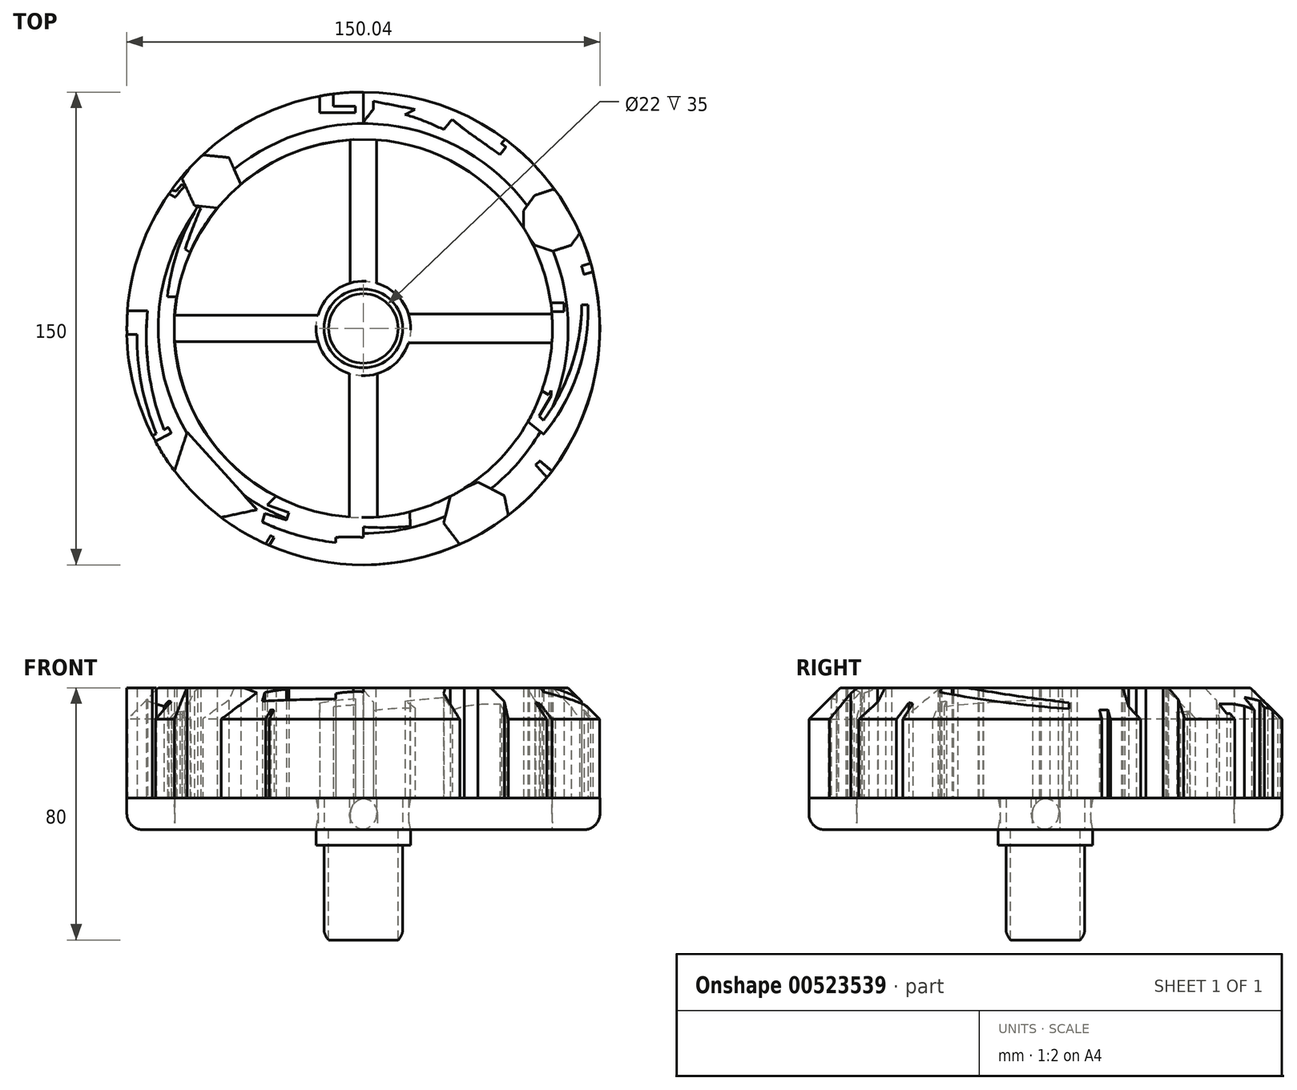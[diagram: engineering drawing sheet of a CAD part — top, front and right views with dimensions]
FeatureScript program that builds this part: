
annotation { "Feature Type Name" : "Feature", "Feature Type Description" : "" }
export const myFeature = defineFeature(function(context is Context, id is Id, definition is map)
    precondition{}
    {
        {
            var Q0;
            Q0=qCreatedBy(makeId("Top.planeOp"),FACE);
            var sketch = newSketch(context, id + "F0", { "sketchPlane" : qUnion([Q0])});
            skCircle(sketch, "E0", {"center": v(-0.06, 0) * mm, "radius": 75 * mm});
            skArc(sketch, "E1", {"start": v(-3.12, 59.92) * mm, "mid": v(-42.12, 42.8) * mm, "end": v(-59.92, 4.1) * mm});
            skArc(sketch, "E2.trimOffspring", {"start": v(59.92, 1.45) * mm, "mid": v(43.26, 41.51) * mm, "end": v(3.94, 59.87) * mm});
            skArc(sketch, "E3.trimOffspring", {"start": v(3.47, -59.9) * mm, "mid": v(43.1, -41.68) * mm, "end": v(59.92, -1.45) * mm});
            skArc(sketch, "E4.trimOffspring", {"start": v(-59.92, -4.1) * mm, "mid": v(-42.29, -42.63) * mm, "end": v(-3.6, -59.9) * mm});
            skLineSegment(sketch, "E5", {"start": v(-3.6, -59.9) * mm, "end": v(3.47, -59.9) * mm});
            skLineSegment(sketch, "E6", {"start": v(-59.92, 4.1) * mm, "end": v(-59.92, -4.1) * mm});
            skLineSegment(sketch, "E7", {"start": v(-3.12, 59.92) * mm, "end": v(3.94, 59.87) * mm});
            skLineSegment(sketch, "E8", {"start": v(59.92, 1.45) * mm, "end": v(59.92, -1.45) * mm});
            skLineSegment(sketch, "E9", {"start": v(-75.04, -1.85) * mm, "end": v(-71.81, -1.85) * mm});
            skArc(sketch, "E10", {"start": v(-71.81, -1.85) * mm, "mid": v(-70.32, -18.07) * mm, "end": v(-65.5, -33.64) * mm});
            skLineSegment(sketch, "E11", {"start": v(-65.5, -33.64) * mm, "end": v(-62.98, -32.75) * mm});
            skArc(sketch, "E12", {"start": v(-68.45, 5.56) * mm, "mid": v(-68, -13.92) * mm, "end": v(-62.98, -32.75) * mm});
            skLineSegment(sketch, "E13", {"start": v(-68.45, 5.56) * mm, "end": v(-74.86, 5.56) * mm});
            skLineSegment(sketch, "E14", {"start": v(-59.2, 10.09) * mm, "end": v(-62.16, 10.09) * mm});
            skArc(sketch, "E15", {"start": v(-52.57, 38.7) * mm, "mid": v(-58.84, 24.89) * mm, "end": v(-62.16, 10.09) * mm});
            skLineSegment(sketch, "E16", {"start": v(-52.57, 38.7) * mm, "end": v(-51.6, 38.07) * mm});
            skArc(sketch, "E17", {"start": v(-51.6, 38.07) * mm, "mid": v(-54.22, 31.64) * mm, "end": v(-56.54, 25.1) * mm});
            skCircle(sketch, "E18.cCircle", {"center": v(-51.93, -51.6) * mm, "radius": 9.56 * mm, "construction": true});
            skLineSegment(sketch, "E18.0", {"start": v(-55.9, -32.91) * mm, "end": v(-33.75, -57.52) * mm});
            skLineSegment(sketch, "E18.1", {"start": v(-33.75, -57.52) * mm, "end": v(-66.13, -64.4) * mm});
            skLineSegment(sketch, "E18.2", {"start": v(-66.13, -64.4) * mm, "end": v(-55.9, -32.91) * mm});
            skPoint(sketch, "E18.0.midPoint", {"position": v(-44.82, -45.21) * mm});
            skLineSegment(sketch, "E19", {"start": v(-27.68, -53.26) * mm, "end": v(-30.43, -56) * mm});
            skLineSegment(sketch, "E20", {"start": v(-23.66, -58.36) * mm, "end": v(-24.37, -60.74) * mm});
            skLineSegment(sketch, "E21", {"start": v(-24.37, -60.74) * mm, "end": v(-31.28, -58.71) * mm});
            skLineSegment(sketch, "E22", {"start": v(-31.28, -58.71) * mm, "end": v(-32.06, -61.39) * mm});
            skArc(sketch, "E23", {"start": v(-32.06, -61.39) * mm, "mid": v(-20.7, -65.62) * mm, "end": v(-8.8, -67.96) * mm});
            skLineSegment(sketch, "E24", {"start": v(-8.8, -67.96) * mm, "end": v(-8.8, -66.27) * mm});
            skArc(sketch, "E25", {"start": v(0, -66.27) * mm, "mid": v(-4.4, -66.16) * mm, "end": v(-8.8, -66.27) * mm});
            skLineSegment(sketch, "E26", {"start": v(0, -66.27) * mm, "end": v(0, -62.95) * mm});
            skArc(sketch, "E27", {"start": v(0, -62.95) * mm, "mid": v(5.89, -63.2) * mm, "end": v(11.77, -62.95) * mm});
            skLineSegment(sketch, "E28", {"start": v(11.77, -62.95) * mm, "end": v(14.82, -62.7) * mm});
            skLineSegment(sketch, "E29", {"start": v(14.82, -62.7) * mm, "end": v(14.7, -58.15) * mm});
            skCircle(sketch, "E30.cCircle", {"center": v(36.07, -59.58) * mm, "radius": 9.76 * mm, "construction": true});
            skLineSegment(sketch, "E30.0", {"start": v(27.76, -52.62) * mm, "end": v(36.33, -48.75) * mm});
            skLineSegment(sketch, "E30.1", {"start": v(36.33, -48.75) * mm, "end": v(44.7, -53.03) * mm});
            skLineSegment(sketch, "E30.2", {"start": v(44.7, -53.03) * mm, "end": v(46.57, -62.25) * mm});
            skLineSegment(sketch, "E30.3", {"start": v(46.57, -62.25) * mm, "end": v(40.53, -69.45) * mm});
            skLineSegment(sketch, "E30.4", {"start": v(40.53, -69.45) * mm, "end": v(31.13, -69.23) * mm});
            skLineSegment(sketch, "E30.5", {"start": v(31.13, -69.23) * mm, "end": v(25.45, -61.74) * mm});
            skLineSegment(sketch, "E30.6", {"start": v(25.45, -61.74) * mm, "end": v(27.76, -52.62) * mm});
            skPoint(sketch, "E30.0.midPoint", {"position": v(32.05, -50.69) * mm});
            skLineSegment(sketch, "E31", {"start": v(58.18, -47.25) * mm, "end": v(54.6, -43.25) * mm});
            skLineSegment(sketch, "E32", {"start": v(54.6, -43.25) * mm, "end": v(55.97, -42.03) * mm});
            skLineSegment(sketch, "E33", {"start": v(55.97, -42.03) * mm, "end": v(59.75, -45.25) * mm});
            skLineSegment(sketch, "E34", {"start": v(52.16, -29.54) * mm, "end": v(57.17, -33.54) * mm});
            skArc(sketch, "E35", {"start": v(57.17, -33.54) * mm, "mid": v(67.92, -14.28) * mm, "end": v(71.22, 7.53) * mm});
            skLineSegment(sketch, "E36", {"start": v(71.22, 7.53) * mm, "end": v(69.25, 7.53) * mm});
            skArc(sketch, "E37", {"start": v(57.08, -29.17) * mm, "mid": v(66.08, -11.78) * mm, "end": v(69.25, 7.53) * mm});
            skLineSegment(sketch, "E38", {"start": v(57.08, -29.17) * mm, "end": v(55.76, -27.85) * mm});
            skLineSegment(sketch, "E39", {"start": v(55.76, -27.85) * mm, "end": v(59.54, -21.34) * mm});
            skLineSegment(sketch, "E40", {"start": v(59.54, -21.34) * mm, "end": v(59.54, -19.73) * mm});
            skLineSegment(sketch, "E41", {"start": v(58.8, -21.06) * mm, "end": v(59.54, -19.73) * mm});
            skLineSegment(sketch, "E42", {"start": v(58.8, -21.06) * mm, "end": v(56.57, -19.82) * mm});
            skLineSegment(sketch, "E43", {"start": v(59.7, 5.3) * mm, "end": v(63.56, 5.3) * mm});
            skLineSegment(sketch, "E44", {"start": v(63.56, 5.3) * mm, "end": v(63.56, 8.1) * mm});
            skLineSegment(sketch, "E45", {"start": v(63.56, 8.1) * mm, "end": v(59.4, 8.1) * mm});
            skCircle(sketch, "E46.cCircle", {"center": v(60.08, 34.31) * mm, "radius": 9.31 * mm, "construction": true});
            skLineSegment(sketch, "E46.0", {"start": v(54.36, 26.37) * mm, "end": v(50.78, 31.25) * mm});
            skLineSegment(sketch, "E46.1", {"start": v(50.78, 31.25) * mm, "end": v(50.76, 37.3) * mm});
            skLineSegment(sketch, "E46.2", {"start": v(50.76, 37.3) * mm, "end": v(54.3, 42.21) * mm});
            skLineSegment(sketch, "E46.3", {"start": v(54.3, 42.21) * mm, "end": v(60.05, 44.1) * mm});
            skLineSegment(sketch, "E46.4", {"start": v(60.05, 44.1) * mm, "end": v(65.8, 42.25) * mm});
            skLineSegment(sketch, "E46.5", {"start": v(65.8, 42.25) * mm, "end": v(69.38, 37.37) * mm});
            skLineSegment(sketch, "E46.6", {"start": v(69.38, 37.37) * mm, "end": v(69.4, 31.32) * mm});
            skLineSegment(sketch, "E46.7", {"start": v(69.4, 31.32) * mm, "end": v(65.87, 26.41) * mm});
            skLineSegment(sketch, "E46.8", {"start": v(65.87, 26.41) * mm, "end": v(60.12, 24.52) * mm});
            skLineSegment(sketch, "E46.9", {"start": v(60.12, 24.52) * mm, "end": v(54.36, 26.37) * mm});
            skPoint(sketch, "E46.0.midPoint", {"position": v(52.57, 28.81) * mm});
            skLineSegment(sketch, "E47", {"start": v(72.04, 20.65) * mm, "end": v(69.17, 19.85) * mm});
            skLineSegment(sketch, "E48", {"start": v(69.17, 19.85) * mm, "end": v(69.92, 17.15) * mm});
            skLineSegment(sketch, "E49", {"start": v(69.92, 17.15) * mm, "end": v(72.76, 17.95) * mm});
            skLineSegment(sketch, "E50", {"start": v(-29.91, -68.8) * mm, "end": v(-28.39, -66.32) * mm});
            skLineSegment(sketch, "E51", {"start": v(-28.39, -66.32) * mm, "end": v(-29.4, -65.7) * mm});
            skLineSegment(sketch, "E52", {"start": v(-29.4, -65.7) * mm, "end": v(-31, -68.32) * mm});
            skLineSegment(sketch, "E53", {"start": v(-66.9, -34) * mm, "end": v(-61.84, -31.39) * mm});
            skLineSegment(sketch, "E54", {"start": v(-61.84, -31.39) * mm, "end": v(-60.9, -33.2) * mm});
            skLineSegment(sketch, "E55", {"start": v(-60.9, -33.2) * mm, "end": v(-65.96, -35.8) * mm});
            skCircle(sketch, "E56.cCircle", {"center": v(-48.13, 46.59) * mm, "radius": 8.14 * mm, "construction": true});
            skLineSegment(sketch, "E56.0", {"start": v(-57.48, 47.52) * mm, "end": v(-52, 55.15) * mm});
            skLineSegment(sketch, "E56.1", {"start": v(-52, 55.15) * mm, "end": v(-42.65, 54.21) * mm});
            skLineSegment(sketch, "E56.2", {"start": v(-42.65, 54.21) * mm, "end": v(-38.79, 45.65) * mm});
            skLineSegment(sketch, "E56.3", {"start": v(-38.79, 45.65) * mm, "end": v(-44.27, 38.02) * mm});
            skLineSegment(sketch, "E56.4", {"start": v(-44.27, 38.02) * mm, "end": v(-53.62, 38.96) * mm});
            skLineSegment(sketch, "E56.5", {"start": v(-53.62, 38.96) * mm, "end": v(-57.48, 47.52) * mm});
            skPoint(sketch, "E56.0.midPoint", {"position": v(-54.74, 51.34) * mm});
            skLineSegment(sketch, "E57", {"start": v(-56.54, 25.1) * mm, "end": v(-55, 24.11) * mm});
            skLineSegment(sketch, "E58", {"start": v(-61.7, 42.74) * mm, "end": v(-59.66, 41.61) * mm});
            skLineSegment(sketch, "E59", {"start": v(-59.66, 41.61) * mm, "end": v(-58.14, 43.52) * mm});
            skLineSegment(sketch, "E60", {"start": v(-58.14, 43.52) * mm, "end": v(-56.83, 45) * mm});
            skLineSegment(sketch, "E61", {"start": v(-56.83, 45) * mm, "end": v(-57.59, 45.67) * mm});
            skLineSegment(sketch, "E62", {"start": v(-57.59, 45.67) * mm, "end": v(-59.43, 43.57) * mm});
            skLineSegment(sketch, "E63", {"start": v(-59.43, 43.57) * mm, "end": v(-60.85, 43.92) * mm});
            skLineSegment(sketch, "E64", {"start": v(45.17, 57.51) * mm, "end": v(43.33, 55.14) * mm});
            skLineSegment(sketch, "E65", {"start": v(43.33, 55.14) * mm, "end": v(32.11, 63.08) * mm});
            skLineSegment(sketch, "E66", {"start": v(0, 65.39) * mm, "end": v(0, 75) * mm});
            skArc(sketch, "E67", {"start": v(3.13, 69.5) * mm, "mid": v(1.52, 67.47) * mm, "end": v(0, 65.39) * mm});
            skLineSegment(sketch, "E68", {"start": v(3.13, 69.5) * mm, "end": v(3.13, 72.11) * mm});
            skLineSegment(sketch, "E69", {"start": v(3.13, 72.11) * mm, "end": v(16.41, 69.5) * mm});
            skLineSegment(sketch, "E70", {"start": v(16.41, 69.5) * mm, "end": v(13.26, 67.89) * mm});
            skArc(sketch, "E71", {"start": v(25.48, 63.08) * mm, "mid": v(19.47, 65.74) * mm, "end": v(13.26, 67.89) * mm});
            skLineSegment(sketch, "E72", {"start": v(25.48, 63.08) * mm, "end": v(28.14, 66.33) * mm});
            skLineSegment(sketch, "E73", {"start": v(28.14, 66.33) * mm, "end": v(32.11, 63.08) * mm});
            skLineSegment(sketch, "E74", {"start": v(65.58, 40.81) * mm, "end": v(66.25, 41.64) * mm});
            skLineSegment(sketch, "E75", {"start": v(62.54, 43.3) * mm, "end": v(65.58, 40.81) * mm});
            skLineSegment(sketch, "E76", {"start": v(43.79, 58.64) * mm, "end": v(44.91, 60.02) * mm});
            skLineSegment(sketch, "E77", {"start": v(-9.57, 74.4) * mm, "end": v(-9.57, 70.46) * mm});
            skLineSegment(sketch, "E78", {"start": v(-9.57, 70.46) * mm, "end": v(-2.58, 70.46) * mm});
            skLineSegment(sketch, "E79", {"start": v(-2.58, 70.46) * mm, "end": v(-2.58, 68.43) * mm});
            skLineSegment(sketch, "E80", {"start": v(-2.58, 68.43) * mm, "end": v(-9.37, 68.43) * mm});
            skLineSegment(sketch, "E81", {"start": v(-9.37, 68.43) * mm, "end": v(-13.9, 68.43) * mm});
            skLineSegment(sketch, "E82", {"start": v(-13.9, 68.43) * mm, "end": v(-13.9, 73.71) * mm});
            skArc(sketch, "E83", {"start": v(-27.44, 58.39) * mm, "mid": v(-46.31, 48.67) * mm, "end": v(-54.8, 29.21) * mm});
            skLineSegment(sketch, "E84", {"start": v(-27.44, 58.39) * mm, "end": v(-27.44, 62.14) * mm});
            skArc(sketch, "E85", {"start": v(-27.44, 62.14) * mm, "mid": v(-37.43, 59.53) * mm, "end": v(-46.73, 55.07) * mm});
            skLineSegment(sketch, "E86.trimOffspring", {"start": v(43.79, 58.64) * mm, "end": v(45.17, 57.51) * mm});
            skLineSegment(sketch, "E87", {"start": v(-30.43, -56) * mm, "end": v(-23.66, -58.36) * mm});
            skSolve(sketch);
        }
        {
            var Q0;
            Q0=qCreatedBy(makeId("Top.planeOp"),FACE);
            var sketch = newSketch(context, id + "F1", { "sketchPlane" : qUnion([Q0])});
            skCircle(sketch, "E88", {"center": v(0, 0) * mm, "radius": 11 * mm});
            skCircle(sketch, "E89", {"center": v(0, 0) * mm, "radius": 12.5 * mm});
            skCircle(sketch, "E90", {"center": v(0, 0) * mm, "radius": 75 * mm});
            skCircle(sketch, "E91", {"center": v(0, 0) * mm, "radius": 60 * mm});
            skLineSegment(sketch, "E92", {"start": v(-11.79, 4.17) * mm, "end": v(-59.86, 4.17) * mm});
            skLineSegment(sketch, "E93", {"start": v(-11.79, -4.17) * mm, "end": v(-59.86, -4.17) * mm});
            skLineSegment(sketch, "E94", {"start": v(-4.17, 59.86) * mm, "end": v(-4.17, 11.79) * mm});
            skLineSegment(sketch, "E95", {"start": v(4.17, 11.79) * mm, "end": v(4.17, 59.86) * mm});
            skLineSegment(sketch, "E96.MirrorCS", {"start": v(11.58, 4.52) * mm, "end": v(59.83, 4.52) * mm});
            skLineSegment(sketch, "E97.MirrorCS", {"start": v(11.58, -4.52) * mm, "end": v(59.83, -4.52) * mm});
            skLineSegment(sketch, "E98.MirrorCS", {"start": v(-4.47, -59.83) * mm, "end": v(-4.41, -11.7) * mm});
            skLineSegment(sketch, "E99.MirrorCS", {"start": v(4.41, -11.7) * mm, "end": v(4.47, -59.83) * mm});
            skSolve(sketch);
        }
        {
            var Q0;
            Q0=qCreatedBy(makeId("Top.planeOp"),FACE);
            var sketch = newSketch(context, id + "F2", { "sketchPlane" : qUnion([Q0])});
            skCircle(sketch, "E100", {"center": v(0, 0) * mm, "radius": 12.5 * mm});
            skCircle(sketch, "E101", {"center": v(0, 0) * mm, "radius": 15 * mm});
            skSolve(sketch);
        }
        {
            var Q0;
            Q0=qCreatedBy(makeId("Top.planeOp"),FACE);
            var sketch = newSketch(context, id + "F3", { "sketchPlane" : qUnion([Q0])});
            skCircle(sketch, "E102", {"center": v(0, 0) * mm, "radius": 11 * mm});
            skCircle(sketch, "E103", {"center": v(0, 0) * mm, "radius": 12.5 * mm});
            skSolve(sketch);
        }
        {
            var Q0;
            {var subQ9=sQuery(id+"F0.wireOp",EDGE,"E6");Q0=makeQuery(id+"F0.imprint","IMPRINT",FACE,{"disambiguationData":[TD([[makeQuery(id+"F0.imprint","IMPRINT",EDGE,{"derivedFrom":subQ9}),-1.0]])]});}
            var Q1;
            {var subQ12=sQuery(id+"F0.wireOp",EDGE,"E7");Q1=makeQuery(id+"F0.imprint","IMPRINT",FACE,{"disambiguationData":[TD([[makeQuery(id+"F0.imprint","IMPRINT",EDGE,{"derivedFrom":subQ12}),1.0]])]});}
            var Q2;
            {var subQ7=sQuery(id+"F0.wireOp",EDGE,"E8");Q2=makeQuery(id+"F0.imprint","IMPRINT",FACE,{"disambiguationData":[TD([[makeQuery(id+"F0.imprint","IMPRINT",EDGE,{"derivedFrom":subQ7}),1.0]])]});}
            var Q3;
            {var subQ0=sQuery(id+"F0.wireOp",EDGE,"E9");Q3=makeQuery(id+"F0.imprint","IMPRINT",FACE,{"disambiguationData":[TD([[makeQuery(id+"F0.imprint","IMPRINT",EDGE,{"derivedFrom":subQ0}),-1.0]])]});}
            var Q4;
            {var subQ1=sQuery(id+"F0.wireOp",EDGE,"E16");Q4=makeQuery(id+"F0.imprint","IMPRINT",FACE,{"disambiguationData":[TD([[makeQuery(id+"F0.imprint","IMPRINT",EDGE,{"derivedFrom":subQ1}),1.0]])]});}
            extrude(context, id + "F4", {"entities" : qUnion([Q0, Q1, Q2, Q3, Q4]), "depth" : 45 * mm, "offsetDistance" : 25 * mm, "hasSecondDirection" : true, "secondDirectionOppositeDirection" : false, "secondDirectionDepth" : 10 * mm});
        }
        {
            var Q0;
            Q0=makeQuery(id+"F2.imprint","IMPRINT",FACE,{"disambiguationData":[TD([[makeQuery(id+"F2.imprint","IMPRINT",EDGE,{"derivedFrom":sQuery(id+"F2.wireOp",EDGE,"E100")}),-1.0]])]});
            var Q1;
            {var subQ0=sQuery(id+"F1.wireOp",EDGE,"E94");Q1=makeQuery(id+"F1.imprint","IMPRINT",FACE,{"disambiguationData":[TD([[makeQuery(id+"F1.imprint","IMPRINT",EDGE,{"derivedFrom":subQ0}),1.0]])]});}
            var Q2;
            {var subQ0=sQuery(id+"F1.wireOp",EDGE,"E92");Q2=makeQuery(id+"F1.imprint","IMPRINT",FACE,{"disambiguationData":[TD([[makeQuery(id+"F1.imprint","IMPRINT",EDGE,{"derivedFrom":subQ0}),1.0]])]});}
            var Q3;
            Q3=makeQuery(id+"F1.imprint","IMPRINT",FACE,{"disambiguationData":[TD([[makeQuery(id+"F1.imprint","IMPRINT",EDGE,{"derivedFrom":sQuery(id+"F1.wireOp",EDGE,"E90")}),1.0]])]});
            var Q4;
            {var subQ0=sQuery(id+"F1.wireOp",EDGE,"E96.MirrorCS");var subQ1=sQuery(id+"F1.wireOp",EDGE,"E89");var subQ2=makeQuery(id+"F1.imprint","INTERSECT",VERTEX,{"derivedFrom":[subQ1,subQ0]});Q4=makeQuery(id+"F1.imprint","IMPRINT",FACE,{"disambiguationData":[TD([[makeQuery(id+"F1.imprint","IMPRINT",EDGE,{"disambiguationData":[TD([[subQ2,1.0]])],"derivedFrom":subQ1}),-1.0]])]});}
            var Q5;
            {var subQ0=sQuery(id+"F1.wireOp",EDGE,"E98.MirrorCS");Q5=makeQuery(id+"F1.imprint","IMPRINT",FACE,{"disambiguationData":[TD([[makeQuery(id+"F1.imprint","IMPRINT",EDGE,{"derivedFrom":subQ0}),-1.0]])]});}
            extrude(context, id + "F5", {"entities" : qUnion([Q0, Q1, Q2, Q3, Q4, Q5]), "operationType" : NewBodyOperationType.ADD, "depth" : 10 * mm, "offsetDistance" : 25 * mm});
        }
        {
            var Q0;
            Q0 = qSketchRegion(id + "F2", true);
            extrude(context, id + "F6", {"entities" : qUnion([Q0]), "operationType" : NewBodyOperationType.ADD, "oppositeDirection" : true, "depth" : 5 * mm, "offsetDistance" : 25 * mm});
        }
        {
            var Q0;
            Q0 = qSketchRegion(id + "F3", true);
            extrude(context, id + "F7", {"entities" : qUnion([Q0]), "operationType" : NewBodyOperationType.ADD, "oppositeDirection" : true, "depth" : 35 * mm, "offsetDistance" : 25 * mm});
        }
        {
            var Q0;
            Q0=makeQuery(id+"F5.opExtrude","CAP_EDGE",EDGE,{"disambiguationData":[OSD([sQuery(id+"F1.wireOp",EDGE,"E93")])],"isStart":false});
            var Q1;
            {var subQ0=sQuery(id+"F2.wireOp",EDGE,"E101");var subQ1=sQuery(id+"F1.wireOp",EDGE,"E92");var subQ2=sQuery(id+"F1.wireOp",EDGE,"E91");var subQ3=sQuery(id+"F1.wireOp",EDGE,"E94");var subQ4=makeQuery(id+"F5.opExtrude","SWEPT_FACE",FACE,{"disambiguationData":[OSD([subQ1])]});var subQ5=makeQuery(id+"F5.opExtrude","CAP_FACE",FACE,{"disambiguationData":[OSD([sQuery(id+"F1.wireOp",EDGE,"E88"),sQuery(id+"F1.wireOp",EDGE,"E89"),sQuery(id+"F1.wireOp",EDGE,"E90"),subQ2,subQ1,sQuery(id+"F1.wireOp",EDGE,"E93"),subQ3,sQuery(id+"F1.wireOp",EDGE,"E95"),sQuery(id+"F1.wireOp",EDGE,"E96.MirrorCS"),sQuery(id+"F1.wireOp",EDGE,"E97.MirrorCS"),sQuery(id+"F1.wireOp",EDGE,"E98.MirrorCS"),sQuery(id+"F1.wireOp",EDGE,"E99.MirrorCS")])],"isStart":true});Q1=makeQuery(id+"F6.boolean.opBoolean","SPLIT",EDGE,{"disambiguationData":[topologyDisambiguationEdgeConnected([subQ5,subQ4]),TD([makeQuery(id+"F6.opExtrude","SWEPT_FACE",FACE,{"disambiguationData":[OSD([subQ0])]})])],"derivedFrom":makeQuery(id+"F5.opExtrude","CAP_EDGE",EDGE,{"disambiguationData":[OSD([subQ1])],"isStart":true})});}
            var Q2;
            {var subQ0=sQuery(id+"F1.wireOp",EDGE,"E94");Q2=makeQuery(id+"F5.boolean.opBoolean","SPLIT",EDGE,{"disambiguationData":[topologyDisambiguationEdgeConnected([makeQuery(id+"F5.opExtrude","CAP_FACE",FACE,{"disambiguationData":[OSD([sQuery(id+"F1.wireOp",EDGE,"E88"),sQuery(id+"F1.wireOp",EDGE,"E89"),sQuery(id+"F1.wireOp",EDGE,"E90"),sQuery(id+"F1.wireOp",EDGE,"E91"),sQuery(id+"F1.wireOp",EDGE,"E92"),sQuery(id+"F1.wireOp",EDGE,"E93"),subQ0,sQuery(id+"F1.wireOp",EDGE,"E95"),sQuery(id+"F1.wireOp",EDGE,"E96.MirrorCS"),sQuery(id+"F1.wireOp",EDGE,"E97.MirrorCS"),sQuery(id+"F1.wireOp",EDGE,"E98.MirrorCS"),sQuery(id+"F1.wireOp",EDGE,"E99.MirrorCS")])],"isStart":false})])],"derivedFrom":makeQuery(id+"F5.opExtrude","CAP_EDGE",EDGE,{"disambiguationData":[OSD([subQ0])],"isStart":false})});}
            var Q3;
            {var subQ0=sQuery(id+"F1.wireOp",EDGE,"E95");Q3=makeQuery(id+"F6.boolean.opBoolean","SPLIT",EDGE,{"disambiguationData":[topologyDisambiguationEdgeConnected([makeQuery(id+"F5.opExtrude","CAP_FACE",FACE,{"disambiguationData":[OSD([sQuery(id+"F1.wireOp",EDGE,"E88"),sQuery(id+"F1.wireOp",EDGE,"E89"),sQuery(id+"F1.wireOp",EDGE,"E90"),sQuery(id+"F1.wireOp",EDGE,"E91"),sQuery(id+"F1.wireOp",EDGE,"E92"),sQuery(id+"F1.wireOp",EDGE,"E93"),sQuery(id+"F1.wireOp",EDGE,"E94"),subQ0,sQuery(id+"F1.wireOp",EDGE,"E96.MirrorCS"),sQuery(id+"F1.wireOp",EDGE,"E97.MirrorCS"),sQuery(id+"F1.wireOp",EDGE,"E98.MirrorCS"),sQuery(id+"F1.wireOp",EDGE,"E99.MirrorCS")])],"isStart":true})])],"derivedFrom":makeQuery(id+"F5.opExtrude","CAP_EDGE",EDGE,{"disambiguationData":[OSD([subQ0])],"isStart":true})});}
            var Q4;
            {var subQ0=sQuery(id+"F1.wireOp",EDGE,"E96.MirrorCS");Q4=makeQuery(id+"F5.boolean.opBoolean","SPLIT",EDGE,{"disambiguationData":[topologyDisambiguationEdgeConnected([makeQuery(id+"F5.opExtrude","CAP_FACE",FACE,{"disambiguationData":[OSD([sQuery(id+"F1.wireOp",EDGE,"E88"),sQuery(id+"F1.wireOp",EDGE,"E89"),sQuery(id+"F1.wireOp",EDGE,"E90"),sQuery(id+"F1.wireOp",EDGE,"E91"),sQuery(id+"F1.wireOp",EDGE,"E92"),sQuery(id+"F1.wireOp",EDGE,"E93"),sQuery(id+"F1.wireOp",EDGE,"E94"),sQuery(id+"F1.wireOp",EDGE,"E95"),subQ0,sQuery(id+"F1.wireOp",EDGE,"E97.MirrorCS"),sQuery(id+"F1.wireOp",EDGE,"E98.MirrorCS"),sQuery(id+"F1.wireOp",EDGE,"E99.MirrorCS")])],"isStart":false})])],"derivedFrom":makeQuery(id+"F5.opExtrude","CAP_EDGE",EDGE,{"disambiguationData":[OSD([subQ0])],"isStart":false})});}
            var Q5;
            {var subQ0=sQuery(id+"F1.wireOp",EDGE,"E97.MirrorCS");Q5=makeQuery(id+"F6.boolean.opBoolean","SPLIT",EDGE,{"disambiguationData":[topologyDisambiguationEdgeConnected([makeQuery(id+"F5.opExtrude","CAP_FACE",FACE,{"disambiguationData":[OSD([sQuery(id+"F1.wireOp",EDGE,"E88"),sQuery(id+"F1.wireOp",EDGE,"E89"),sQuery(id+"F1.wireOp",EDGE,"E90"),sQuery(id+"F1.wireOp",EDGE,"E91"),sQuery(id+"F1.wireOp",EDGE,"E92"),sQuery(id+"F1.wireOp",EDGE,"E93"),sQuery(id+"F1.wireOp",EDGE,"E94"),sQuery(id+"F1.wireOp",EDGE,"E95"),sQuery(id+"F1.wireOp",EDGE,"E96.MirrorCS"),subQ0,sQuery(id+"F1.wireOp",EDGE,"E98.MirrorCS"),sQuery(id+"F1.wireOp",EDGE,"E99.MirrorCS")])],"isStart":true})])],"derivedFrom":makeQuery(id+"F5.opExtrude","CAP_EDGE",EDGE,{"disambiguationData":[OSD([subQ0])],"isStart":true})});}
            var Q6;
            Q6=makeQuery(id+"F5.opExtrude","CAP_EDGE",EDGE,{"disambiguationData":[OSD([sQuery(id+"F1.wireOp",EDGE,"E99.MirrorCS")])],"isStart":false});
            var Q7;
            {var subQ0=sQuery(id+"F2.wireOp",EDGE,"E101");var subQ1=sQuery(id+"F1.wireOp",EDGE,"E98.MirrorCS");var subQ2=makeQuery(id+"F5.opExtrude","SWEPT_FACE",FACE,{"disambiguationData":[OSD([subQ1])]});var subQ3=sQuery(id+"F1.wireOp",EDGE,"E93");var subQ4=sQuery(id+"F1.wireOp",EDGE,"E91");var subQ5=makeQuery(id+"F5.opExtrude","CAP_FACE",FACE,{"disambiguationData":[OSD([sQuery(id+"F1.wireOp",EDGE,"E88"),sQuery(id+"F1.wireOp",EDGE,"E89"),sQuery(id+"F1.wireOp",EDGE,"E90"),subQ4,sQuery(id+"F1.wireOp",EDGE,"E92"),subQ3,sQuery(id+"F1.wireOp",EDGE,"E94"),sQuery(id+"F1.wireOp",EDGE,"E95"),sQuery(id+"F1.wireOp",EDGE,"E96.MirrorCS"),sQuery(id+"F1.wireOp",EDGE,"E97.MirrorCS"),subQ1,sQuery(id+"F1.wireOp",EDGE,"E99.MirrorCS")])],"isStart":true});Q7=makeQuery(id+"F6.boolean.opBoolean","SPLIT",EDGE,{"disambiguationData":[topologyDisambiguationEdgeConnected([subQ5,subQ2]),TD([makeQuery(id+"F6.opExtrude","SWEPT_FACE",FACE,{"disambiguationData":[OSD([subQ0])]})])],"derivedFrom":makeQuery(id+"F5.opExtrude","CAP_EDGE",EDGE,{"disambiguationData":[OSD([subQ1])],"isStart":true})});}
            var Q8;
            Q8=makeQuery(id+"F5.opExtrude","CAP_EDGE",EDGE,{"disambiguationData":[OSD([sQuery(id+"F1.wireOp",EDGE,"E90")])],"isStart":true});
            var Q9;
            Q9=makeQuery(id+"F7.opExtrude","CAP_EDGE",EDGE,{"disambiguationData":[OSD([sQuery(id+"F3.wireOp",EDGE,"E103")])],"isStart":false});
            fillet(context, id + "F8", {"entities" : qUnion([Q0, Q1, Q2, Q3, Q4, Q5, Q6, Q7, Q8, Q9]), "radius" : 5 * mm, "tangentPropagation" : true, "allowEdgeOverflow" : false});
        }
        {
            var Q0;
            {var subQ0=sQuery(id+"F0.wireOp",EDGE,"E0");Q0=makeQuery(id+"F4.opExtrude","CAP_EDGE",EDGE,{"disambiguationData":[OSD([subQ0]),TDD([makeQuery(id+"F0.imprint","IMPRINT",EDGE,{"disambiguationData":[TD([[makeQuery(id+"F0.imprint","INTERSECT",VERTEX,{"derivedFrom":[subQ0,sQuery(id+"F0.wireOp",EDGE,"E50")]}),-1.0]])],"derivedFrom":subQ0})])],"isStart":false});}
            var Q1;
            {var subQ0=sQuery(id+"F0.wireOp",EDGE,"E0");Q1=makeQuery(id+"F4.opExtrude","CAP_EDGE",EDGE,{"disambiguationData":[OSD([subQ0]),TDD([makeQuery(id+"F0.imprint","IMPRINT",EDGE,{"disambiguationData":[TD([[makeQuery(id+"F0.imprint","INTERSECT",VERTEX,{"derivedFrom":[subQ0,sQuery(id+"F0.wireOp",EDGE,"E13")]}),1.0]])],"derivedFrom":subQ0})])],"isStart":false});}
            var Q2;
            {var subQ0=sQuery(id+"F0.wireOp",EDGE,"E0");Q2=makeQuery(id+"F4.opExtrude","CAP_EDGE",EDGE,{"disambiguationData":[OSD([subQ0]),TDD([makeQuery(id+"F0.imprint","IMPRINT",EDGE,{"disambiguationData":[TD([[makeQuery(id+"F0.imprint","INTERSECT",VERTEX,{"derivedFrom":[subQ0,sQuery(id+"F0.wireOp",EDGE,"E82")]}),-1.0]])],"derivedFrom":subQ0})])],"isStart":false});}
            var Q3;
            {var subQ0=sQuery(id+"F0.wireOp",EDGE,"E0");Q3=makeQuery(id+"F4.opExtrude","CAP_EDGE",EDGE,{"disambiguationData":[OSD([subQ0]),TDD([makeQuery(id+"F0.imprint","IMPRINT",EDGE,{"disambiguationData":[TD([[makeQuery(id+"F0.imprint","INTERSECT",VERTEX,{"derivedFrom":[subQ0,sQuery(id+"F0.wireOp",EDGE,"E33")]}),-1.0]])],"derivedFrom":subQ0})])],"isStart":false});}
            chamfer(context, id + "F9", {"entities" : qUnion([Q0, Q1, Q2, Q3]), "width" : 10 * mm, "tangentPropagation" : true});
        }
    });
